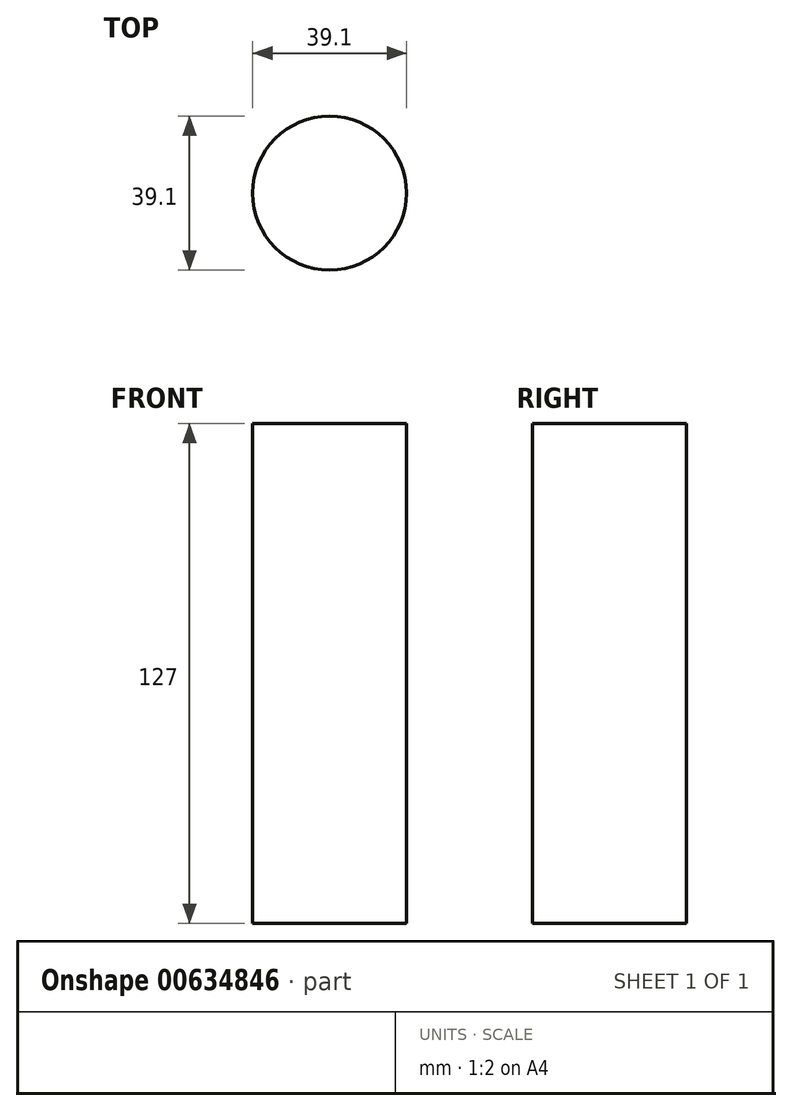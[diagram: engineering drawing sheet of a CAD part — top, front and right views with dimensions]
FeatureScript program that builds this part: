
annotation { "Feature Type Name" : "Feature", "Feature Type Description" : "" }
export const myFeature = defineFeature(function(context is Context, id is Id, definition is map)
    precondition{}
    {
        {
            var Q0;
            Q0=qCreatedBy(makeId("Top.planeOp"),FACE);
            var sketch = newSketch(context, id + "F0", { "sketchPlane" : qUnion([Q0])});
            skCircle(sketch, "E0", {"center": v(0, 0) * mm, "radius": 19.55 * mm});
            skSolve(sketch);
        }
        {
            var Q0;
            Q0=makeQuery(id+"F0.imprint","IMPRINT",FACE,{"disambiguationData":[TD([[makeQuery(id+"F0.imprint","IMPRINT",EDGE,{"derivedFrom":sQuery(id+"F0.wireOp",EDGE,"E0")}),1.0]])]});
            extrude(context, id + "F1", {"entities" : qUnion([Q0]), "depth" : 127 * mm, "offsetDistance" : 25.4 * mm});
        }
    });
